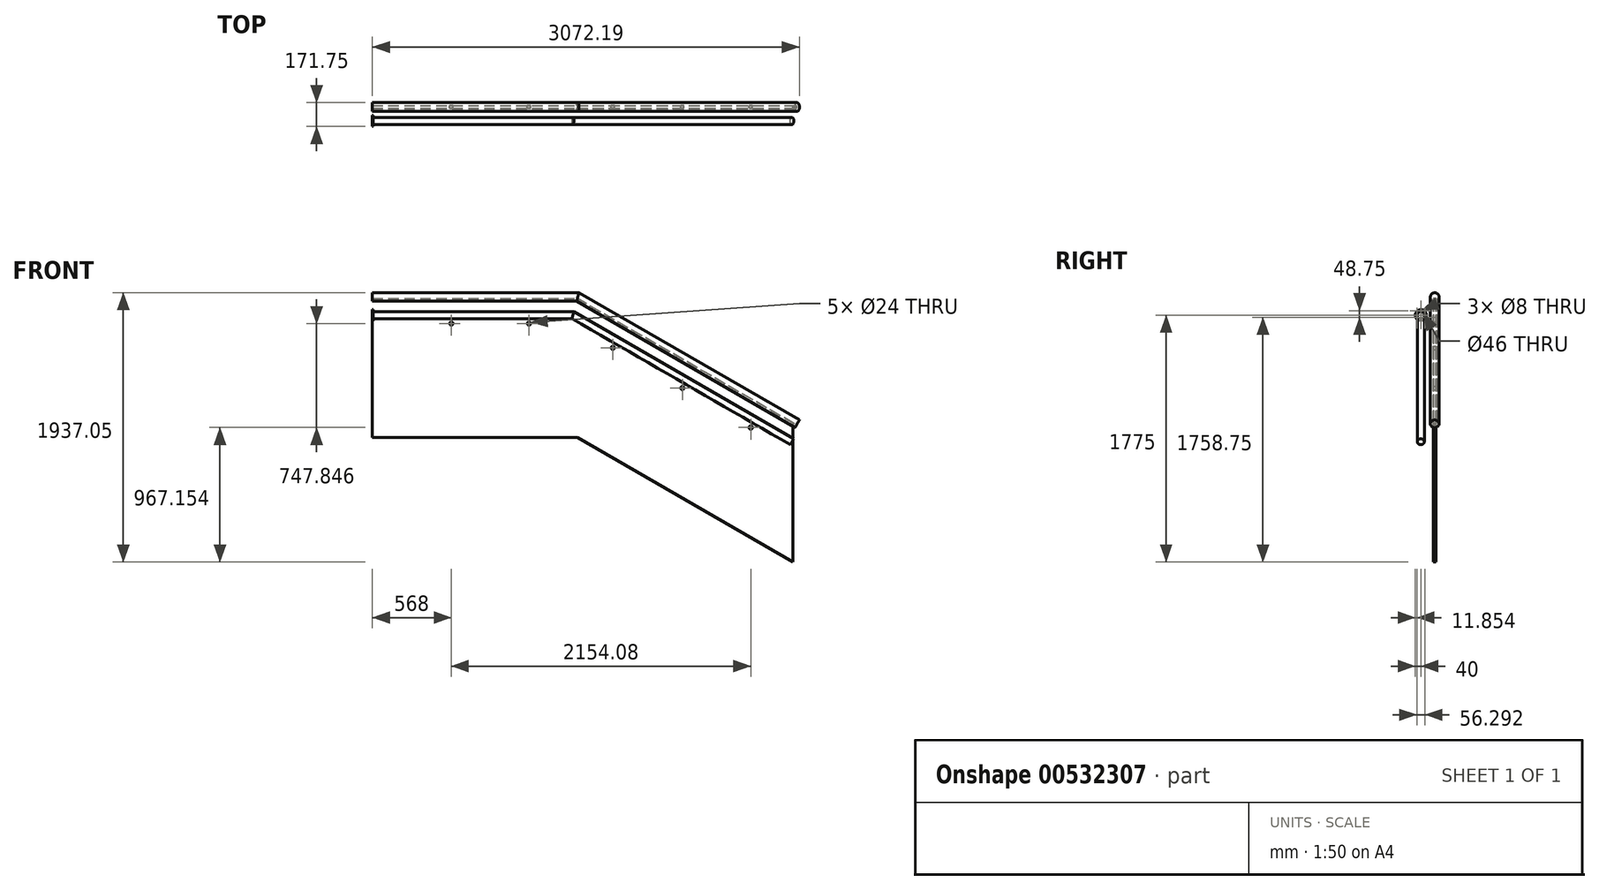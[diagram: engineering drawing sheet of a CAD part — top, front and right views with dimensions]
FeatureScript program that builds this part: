
annotation { "Feature Type Name" : "Feature", "Feature Type Description" : "" }
export const myFeature = defineFeature(function(context is Context, id is Id, definition is map)
    precondition{}
    {
        {
            var Q0;
            Q0=qCreatedBy(makeId("Front.planeOp"),FACE);
            var sketch = newSketch(context, id + "F0", { "sketchPlane" : qUnion([Q0])});
            skLineSegment(sketch, "E0.bottom", {"start": v(0, 0) * mm, "end": v(1475, 0) * mm});
            skLineSegment(sketch, "E0.top", {"start": v(0, 1000) * mm, "end": v(1475, 1000) * mm});
            skLineSegment(sketch, "E0.left", {"start": v(0, 0) * mm, "end": v(0, 1000) * mm});
            skLineSegment(sketch, "E1", {"start": v(1475, 0) * mm, "end": v(3025.19, -895) * mm});
            skLineSegment(sketch, "E2", {"start": v(3025.19, -895) * mm, "end": v(3025.19, 105) * mm});
            skLineSegment(sketch, "E3", {"start": v(3025.19, 105) * mm, "end": v(1475, 1000) * mm});
            skLineSegment(sketch, "E4.0", {"start": v(3025.19, -102.85) * mm, "end": v(1426.77, 820) * mm, "construction": true});
            skLineSegment(sketch, "E4.1", {"start": v(0, 820) * mm, "end": v(1426.77, 820) * mm, "construction": true});
            skCircle(sketch, "E5", {"center": v(568, 820) * mm, "radius": 12 * mm});
            skCircle(sketch, "E6", {"center": v(1126.77, 820) * mm, "radius": 12 * mm});
            skCircle(sketch, "E7", {"center": v(1729.88, 645) * mm, "radius": 12 * mm});
            skCircle(sketch, "E8", {"center": v(2230.17, 356.15) * mm, "radius": 12 * mm});
            skCircle(sketch, "E9", {"center": v(2722.08, 72.15) * mm, "radius": 12 * mm});
            skSolve(sketch);
        }
        {
            var Q0;
            Q0 = qSketchRegion(id + "F0", true);
            extrude(context, id + "F1", {"entities" : qUnion([Q0]), "endBound" : BoundingType.SYMMETRIC, "depth" : 19 * mm, "offsetDistance" : 25 * mm});
        }
        {
            var Q0;
            Q0=qCreatedBy(makeId("Front.planeOp"),FACE);
            var sketch = newSketch(context, id + "F2", { "sketchPlane" : qUnion([Q0])});
            skLineSegment(sketch, "E10.0", {"start": v(0, 1000) * mm, "end": v(1475, 1000) * mm});
            skLineSegment(sketch, "E10.1", {"start": v(3051.17, 90) * mm, "end": v(1475, 1000) * mm});
            skSolve(sketch);
        }
        {
            var Q0;
            Q0=qCreatedBy(makeId("Right.planeOp"),FACE);
            var sketch = newSketch(context, id + "F3", { "sketchPlane" : qUnion([Q0])});
            skLineSegment(sketch, "E11", {"start": v(9.5, 980) * mm, "end": v(9.5, 1000) * mm});
            skLineSegment(sketch, "E12.0", {"start": v(-9.5, 1000) * mm, "end": v(9.5, 1000) * mm});
            skLineSegment(sketch, "E13", {"start": v(-9.5, 1000) * mm, "end": v(-9.5, 980) * mm});
            skArc(sketch, "E14", {"start": v(9.5, 980) * mm, "mid": v(0, 1042.05) * mm, "end": v(-9.5, 980) * mm});
            skArc(sketch, "E15.0", {"start": v(11, 982.12) * mm, "mid": v(0, 1040.55) * mm, "end": v(-11, 982.12) * mm});
            skLineSegment(sketch, "E15.1", {"start": v(11, 982.12) * mm, "end": v(11, 1001.5) * mm});
            skLineSegment(sketch, "E15.2", {"start": v(-11, 1001.5) * mm, "end": v(11, 1001.5) * mm});
            skLineSegment(sketch, "E15.3", {"start": v(-11, 1001.5) * mm, "end": v(-11, 982.12) * mm});
            skSolve(sketch);
        }
        {
            var Q0;
            Q0 = qSketchRegion(id + "F3", true);
            var Q1;
            Q1=sQuery(id+"F2.wireOp",EDGE,"E10.0");
            var Q2;
            Q2=sQuery(id+"F2.wireOp",EDGE,"E10.1");
            sweep(context, id + "F4", {"profiles" : qUnion([Q0]), "path" : qUnion([Q1, Q2])});
        }
        {
            var Q0;
            Q0=makeQuery(id+"F4.opSweep","CAP_FACE",FACE,{"disambiguationData":[OSD([sQuery(id+"F2.wireOp",VERTEX,"E10.1.start"),sQuery(id+"F3.wireOp",EDGE,"E11"),sQuery(id+"F3.wireOp",EDGE,"E12.0"),sQuery(id+"F3.wireOp",EDGE,"E13"),sQuery(id+"F3.wireOp",EDGE,"E14"),sQuery(id+"F3.wireOp",EDGE,"E15.0"),sQuery(id+"F3.wireOp",EDGE,"E15.1"),sQuery(id+"F3.wireOp",EDGE,"E15.2"),sQuery(id+"F3.wireOp",EDGE,"E15.3")])],"isStart":false});
            var sketch = newSketch(context, id + "F5", { "sketchPlane" : qUnion([Q0])});
            skCircle(sketch, "E16", {"center": v(0, 1613.82) * mm, "radius": 31.75 * mm});
            skSolve(sketch);
        }
        {
            var Q0;
            Q0 = qSketchRegion(id + "F5", true);
            extrude(context, id + "F6", {"entities" : qUnion([Q0]), "operationType" : NewBodyOperationType.ADD, "oppositeDirection" : true, "depth" : 2 * mm, "offsetDistance" : 25 * mm});
        }
        {
            var Q0;
            Q0=qCreatedBy(makeId("Front.planeOp"),FACE);
            cPlane(context, id + "F7", {"entities" : qUnion([Q0]), "cplaneType" : CPlaneType.OFFSET, "offset" : 100 * mm, "width" : 150 * mm, "height" : 150 * mm});
        }
        {
            var Q0;
            Q0=qCreatedBy(id+"F7.planeOp",FACE);
            var sketch = newSketch(context, id + "F8", { "sketchPlane" : qUnion([Q0])});
            skLineSegment(sketch, "E17.0", {"start": v(1442.85, 880) * mm, "end": v(3019.01, -30) * mm});
            skLineSegment(sketch, "E17.1", {"start": v(0, 880) * mm, "end": v(1442.85, 880) * mm});
            skSolve(sketch);
        }
        {
            var Q0;
            Q0=qCreatedBy(makeId("Right.planeOp"),FACE);
            var sketch = newSketch(context, id + "F9", { "sketchPlane" : qUnion([Q0])});
            skCircle(sketch, "E18", {"center": v(-100, 880) * mm, "radius": 25 * mm});
            skCircle(sketch, "E19.0", {"center": v(-100, 880) * mm, "radius": 23 * mm});
            skSolve(sketch);
        }
        {
            var Q0;
            Q0=makeQuery(id+"F9.imprint","IMPRINT",FACE,{"disambiguationData":[TD([[makeQuery(id+"F9.imprint","IMPRINT",EDGE,{"derivedFrom":sQuery(id+"F9.wireOp",EDGE,"E18")}),1.0]])]});
            var Q1;
            Q1=sQuery(id+"F8.wireOp",EDGE,"E17.1");
            var Q2;
            Q2=sQuery(id+"F8.wireOp",EDGE,"E17.0");
            sweep(context, id + "F10", {"profiles" : qUnion([Q0]), "path" : qUnion([Q1, Q2])});
        }
        {
            var Q0;
            Q0=qCreatedBy(id+"F7.planeOp",FACE);
            var sketch = newSketch(context, id + "F11", { "sketchPlane" : qUnion([Q0])});
            skLineSegment(sketch, "E20.0", {"start": v(3031.51, -8.35) * mm, "end": v(3019.01, -30) * mm});
            skLineSegment(sketch, "E21", {"start": v(3019.01, -30) * mm, "end": v(3040.66, -42.5) * mm});
            skArc(sketch, "E22", {"start": v(3031.51, -8.35) * mm, "mid": v(3043.16, -23.53) * mm, "end": v(3040.66, -42.5) * mm});
            skLineSegment(sketch, "E23", {"start": v(3019.01, -30) * mm, "end": v(3176.2, -120.75) * mm, "construction": true});
            skPoint(sketch, "E24.orphan", {"position": v(3006.51, -51.65) * mm});
            skSolve(sketch);
        }
        {
            var Q0;
            Q0=makeQuery(id+"F10.opSweep","CAP_FACE",FACE,{"disambiguationData":[OSD([sQuery(id+"F8.wireOp",VERTEX,"E17.0.end"),sQuery(id+"F9.wireOp",EDGE,"E18"),sQuery(id+"F9.wireOp",EDGE,"E19.0")])],"isStart":false});
            var sketch = newSketch(context, id + "F12", { "sketchPlane" : qUnion([Q0])});
            skCircle(sketch, "E25", {"center": v(-100, 1483.53) * mm, "radius": 25 * mm});
            skSolve(sketch);
        }
        {
            var Q0;
            Q0 = qSketchRegion(id + "F12", true);
            extrude(context, id + "F13", {"entities" : qUnion([Q0]), "operationType" : NewBodyOperationType.ADD, "oppositeDirection" : true, "depth" : 3 * mm, "offsetDistance" : 25 * mm});
        }
        {
            var Q0;
            Q0=makeQuery(id+"F10.opSweep","CAP_FACE",FACE,{"disambiguationData":[OSD([sQuery(id+"F8.wireOp",VERTEX,"E17.1.start"),sQuery(id+"F9.wireOp",EDGE,"E18"),sQuery(id+"F9.wireOp",EDGE,"E19.0")])],"isStart":true});
            var sketch = newSketch(context, id + "F14", { "sketchPlane" : qUnion([Q0])});
            skCircle(sketch, "E26.0", {"center": v(100, 880) * mm, "radius": 25 * mm});
            skCircle(sketch, "E27.0", {"center": v(100, 880) * mm, "radius": 40 * mm});
            skCircle(sketch, "E28", {"center": v(100, 912.5) * mm, "radius": 4 * mm});
            skCircle(sketch, "E29", {"center": v(128.15, 863.75) * mm, "radius": 4 * mm});
            skCircle(sketch, "E30", {"center": v(71.85, 863.75) * mm, "radius": 4 * mm});
            skCircle(sketch, "E31", {"center": v(100, 880) * mm, "radius": 32.5 * mm, "construction": true});
            skLineSegment(sketch, "E32", {"start": v(100, 880) * mm, "end": v(128.15, 863.75) * mm, "construction": true});
            skLineSegment(sketch, "E33", {"start": v(100, 880) * mm, "end": v(71.85, 863.75) * mm, "construction": true});
            skLineSegment(sketch, "E34", {"start": v(100, 880) * mm, "end": v(100, 912.5) * mm, "construction": true});
            skSolve(sketch);
        }
        {
            var Q0;
            Q0=makeQuery(id+"F14.imprint","IMPRINT",FACE,{"disambiguationData":[TD([[makeQuery(id+"F14.imprint","IMPRINT",EDGE,{"derivedFrom":sQuery(id+"F14.wireOp",EDGE,"E26.0")}),1.0]])]});
            extrude(context, id + "F15", {"entities" : qUnion([Q0]), "operationType" : NewBodyOperationType.ADD, "oppositeDirection" : true, "depth" : 5 * mm, "offsetDistance" : 25 * mm});
        }
    });
